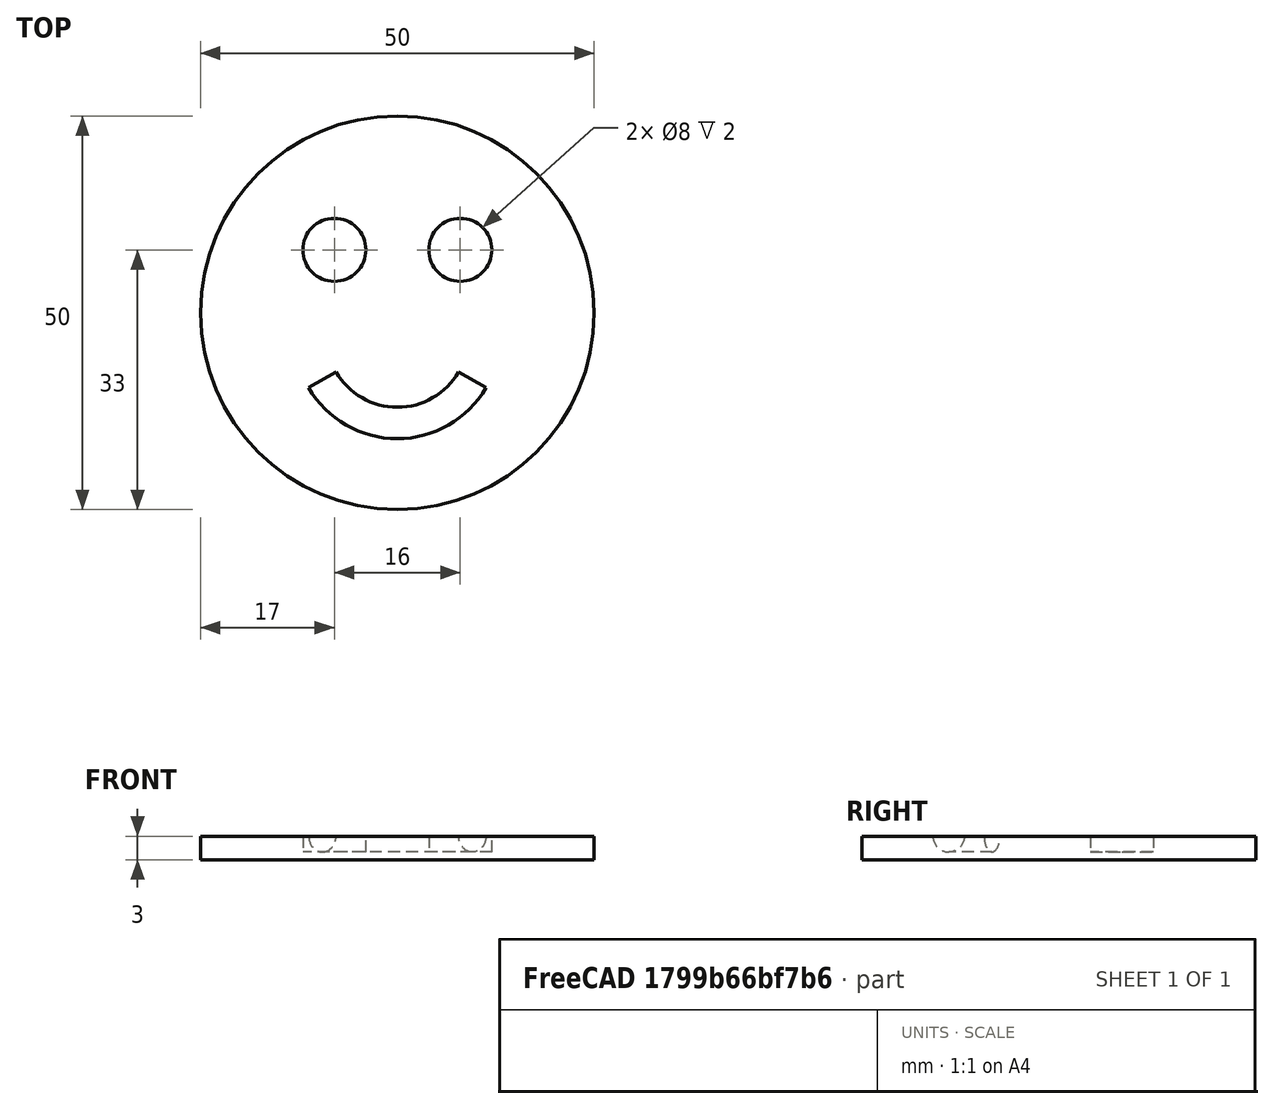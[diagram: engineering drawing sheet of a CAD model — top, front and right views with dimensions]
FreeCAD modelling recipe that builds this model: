
FCSTD DOCUMENT  (FreeCAD 1.0R39319 (Git))
Label: ojt1_t15r01_smile
License: All rights reserved
LicenseURL: https://en.wikipedia.org/wiki/All_rights_reserved
objects: Part::Cylinder×3, Part::MultiFuse×2, Part::Torus×1, Part::Cut×1
note: 7 computed .brp shape members not serialized (recipe doc carries the construction recipe); baked Part::Feature solids carry a one-line shape summary decoded from their .brp

FEATURE [Part::Cylinder] Cylinder
  Angle = 360
  AttacherType = Attacher::AttachEngine3D
  FirstAngle = 0
  Height = 3
  Radius = 25
  SecondAngle = 0
FEATURE [Part::Cylinder] Cylinder001
  Angle = 360
  AttacherType = Attacher::AttachEngine3D
  FirstAngle = 0
  Height = 2
  Placement = pos=(8,0,1) rot=(0,0,1;0rad)
  Radius = 4
  SecondAngle = 0
FEATURE [Part::Cylinder] Cylinder002
  Angle = 360
  AttacherType = Attacher::AttachEngine3D
  FirstAngle = 0
  Height = 2
  Placement = pos=(-8,0,1) rot=(0,0,1;0rad)
  Radius = 4
  SecondAngle = 0
FEATURE [Part::MultiFuse] Fusion
  Placement = pos=(0,8,0) rot=(0,0,1;0rad)
  Refine = true
  Shapes = -> [Cylinder002,Cylinder001]
FEATURE [Part::Torus] Torus
  Angle1 = -180
  Angle2 = 180
  Angle3 = 120
  AttacherType = Attacher::AttachEngine3D
  Placement = pos=(0,-3,3) rot=(0,0,1;-2.61799rad)
  Radius1 = 11
  Radius2 = 2
FEATURE [Part::MultiFuse] Fusion001
  Refine = true
  Shapes = -> [Torus,Fusion]
FEATURE [Part::Cut] Cut
  Base = -> Cylinder
  Refine = true
  Tool = -> Fusion001
